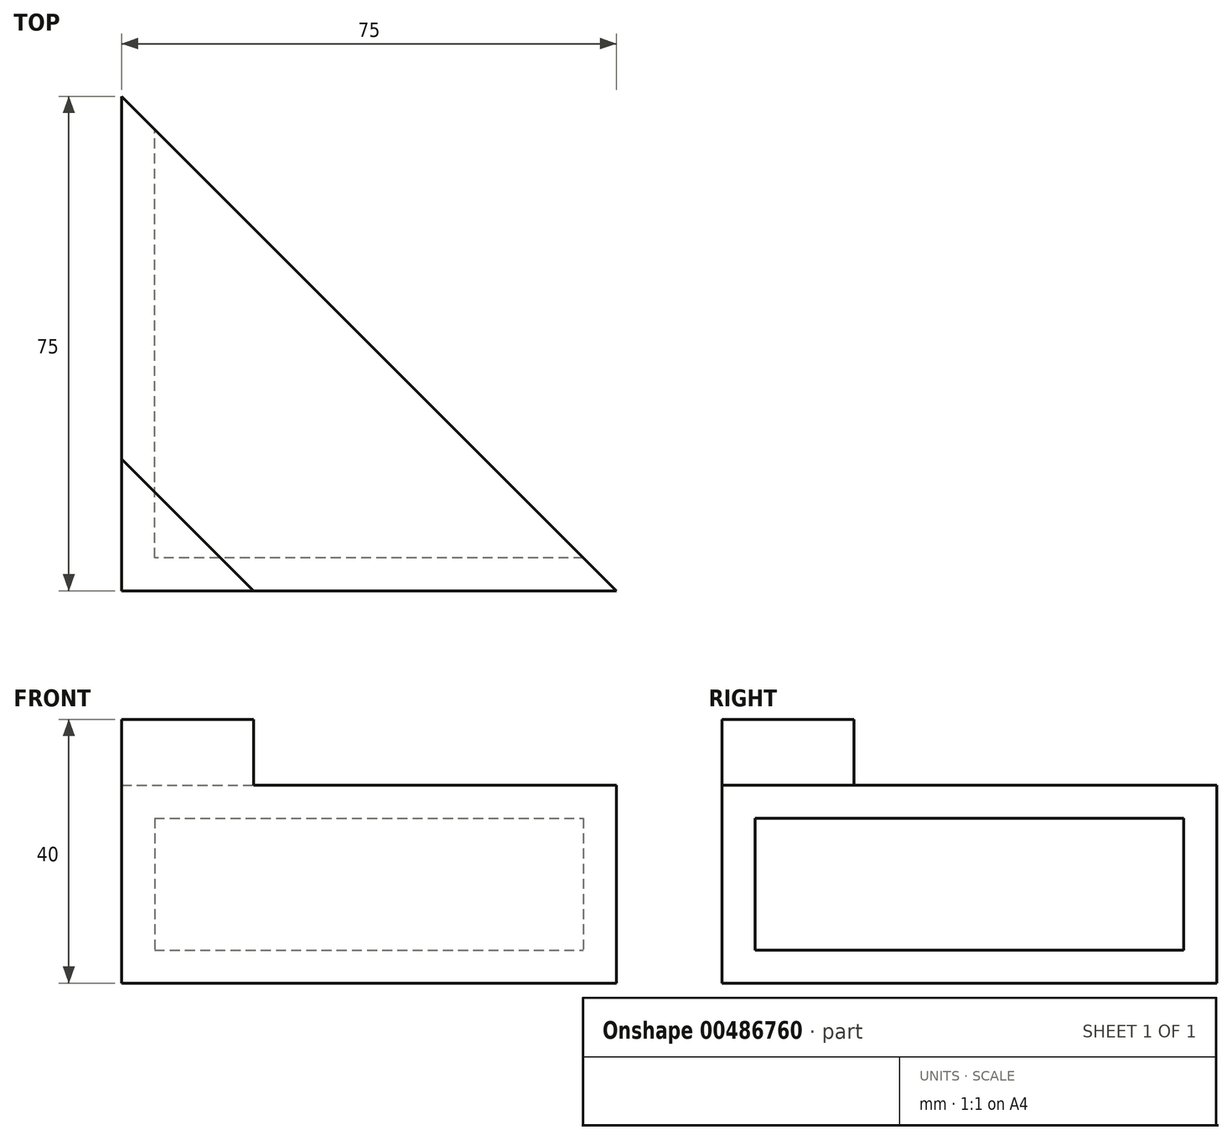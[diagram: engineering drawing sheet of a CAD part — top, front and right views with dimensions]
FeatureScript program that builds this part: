
annotation { "Feature Type Name" : "Feature", "Feature Type Description" : "" }
export const myFeature = defineFeature(function(context is Context, id is Id, definition is map)
    precondition{}
    {
        {
            var Q0;
            Q0=qCreatedBy(makeId("Top.planeOp"),FACE);
            var sketch = newSketch(context, id + "F0", { "sketchPlane" : qUnion([Q0])});
            skLineSegment(sketch, "E0", {"start": v(0, 0) * mm, "end": v(0, 75) * mm});
            skLineSegment(sketch, "E1", {"start": v(0, 75) * mm, "end": v(75, 0) * mm});
            skLineSegment(sketch, "E2", {"start": v(75, 0) * mm, "end": v(0, 0) * mm});
            skSolve(sketch);
        }
        {
            var Q0;
            Q0=makeQuery(id+"F0.imprint","IMPRINT",FACE,{"disambiguationData":[TD([[makeQuery(id+"F0.imprint","IMPRINT",EDGE,{"derivedFrom":sQuery(id+"F0.wireOp",EDGE,"E0")}),-1.0]])]});
            extrude(context, id + "F1", {"entities" : qUnion([Q0]), "depth" : 30 * mm});
        }
        {
            var Q0;
            Q0=makeQuery(id+"F1.opExtrude","SWEPT_FACE",FACE,{"disambiguationData":[OSD([sQuery(id+"F0.wireOp",EDGE,"E1")])]});
            shell(context, id + "F2", {"entities" : qUnion([Q0]), "thickness" : 5 * mm});
        }
        {
            var Q0;
            Q0=makeQuery(id+"F1.opExtrude","CAP_FACE",FACE,{"disambiguationData":[OSD([sQuery(id+"F0.wireOp",EDGE,"E0"),sQuery(id+"F0.wireOp",EDGE,"E1"),sQuery(id+"F0.wireOp",EDGE,"E2")])],"isStart":false});
            var sketch = newSketch(context, id + "F3", { "sketchPlane" : qUnion([Q0])});
            skLineSegment(sketch, "E3", {"start": v(0, 0) * mm, "end": v(0, 20) * mm});
            skLineSegment(sketch, "E4", {"start": v(0, 20) * mm, "end": v(20, 0) * mm});
            skLineSegment(sketch, "E5", {"start": v(20, 0) * mm, "end": v(0, 0) * mm});
            skSolve(sketch);
        }
        {
            var Q0;
            Q0=makeQuery(id+"F3.imprint","IMPRINT",FACE,{"disambiguationData":[TD([[makeQuery(id+"F3.imprint","IMPRINT",EDGE,{"derivedFrom":sQuery(id+"F3.wireOp",EDGE,"E3")}),-1.0]])]});
            extrude(context, id + "F4", {"entities" : qUnion([Q0]), "operationType" : NewBodyOperationType.ADD, "depth" : 10 * mm});
        }
    });
